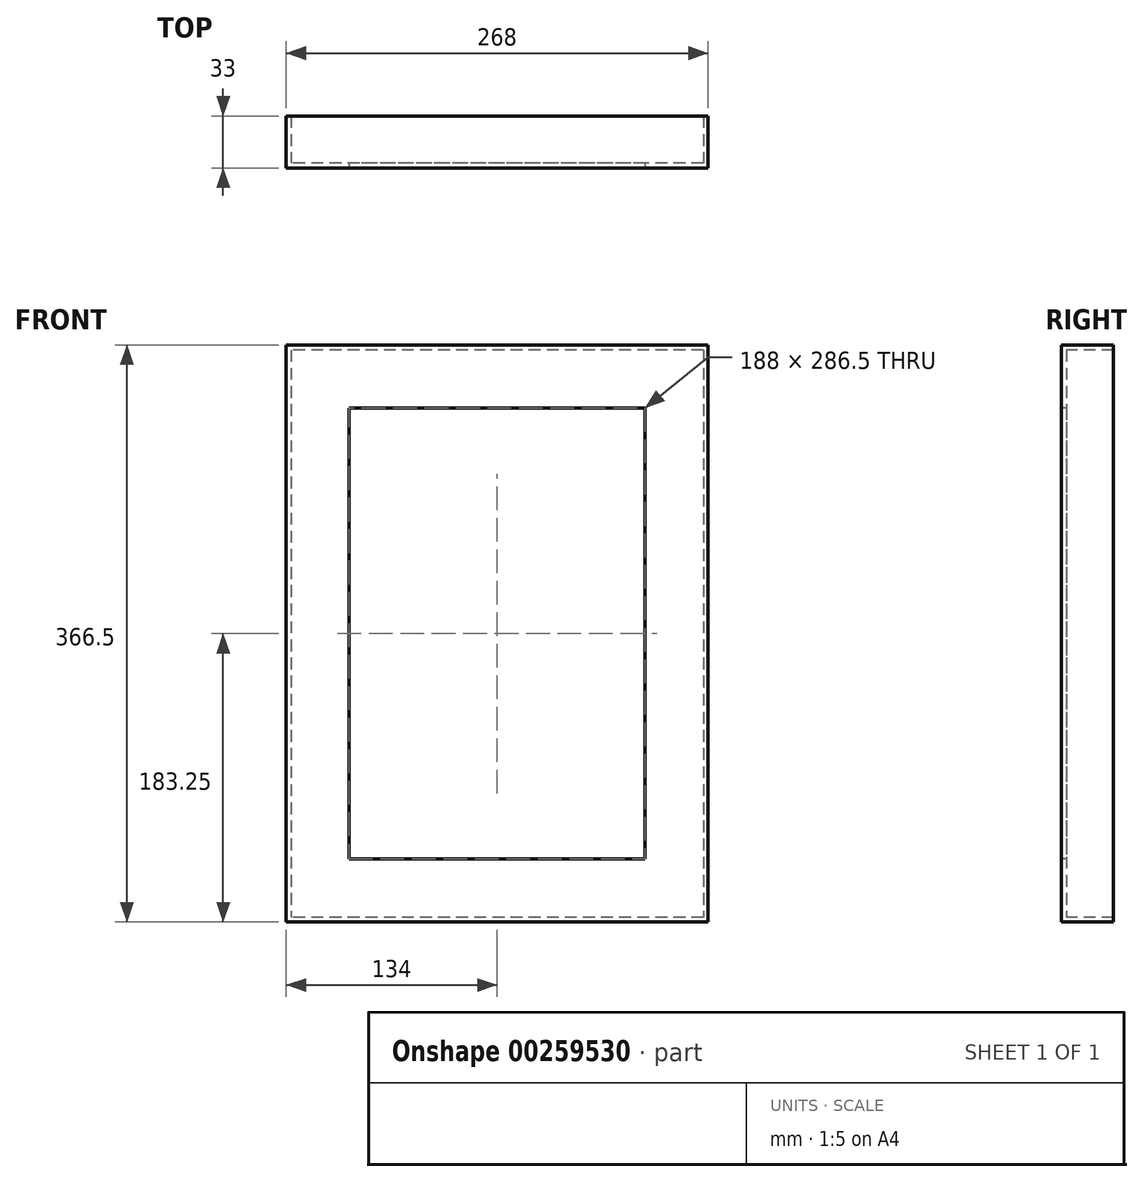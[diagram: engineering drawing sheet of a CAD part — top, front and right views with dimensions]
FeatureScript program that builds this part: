
annotation { "Feature Type Name" : "Feature", "Feature Type Description" : "" }
export const myFeature = defineFeature(function(context is Context, id is Id, definition is map)
    precondition{}
    {
        {
            var Q0;
            Q0=qCreatedBy(makeId("Front.planeOp"),FACE);
            var sketch = newSketch(context, id + "F0", { "sketchPlane" : qUnion([Q0])});
            skLineSegment(sketch, "E0.bottom", {"start": v(94, 143.25) * mm, "end": v(-94, 143.25) * mm});
            skLineSegment(sketch, "E0.top", {"start": v(94, -143.25) * mm, "end": v(-94, -143.25) * mm});
            skLineSegment(sketch, "E0.left", {"start": v(94, 143.25) * mm, "end": v(94, -143.25) * mm});
            skLineSegment(sketch, "E0.right", {"start": v(-94, 143.25) * mm, "end": v(-94, -143.25) * mm});
            skPoint(sketch, "E0.middle", {"position": v(0, 0) * mm});
            skLineSegment(sketch, "E1.0", {"start": v(-134, 183.25) * mm, "end": v(-134, -183.25) * mm});
            skLineSegment(sketch, "E1.1", {"start": v(134, 183.25) * mm, "end": v(-134, 183.25) * mm});
            skLineSegment(sketch, "E1.2", {"start": v(134, 183.25) * mm, "end": v(134, -183.25) * mm});
            skLineSegment(sketch, "E1.3", {"start": v(134, -183.25) * mm, "end": v(-134, -183.25) * mm});
            skSolve(sketch);
        }
        {
            var Q0;
            Q0=makeQuery(id+"F0.imprint","IMPRINT",FACE,{"disambiguationData":[TD([[makeQuery(id+"F0.imprint","IMPRINT",EDGE,{"derivedFrom":sQuery(id+"F0.wireOp",EDGE,"E0.bottom")}),-1.0]])]});
            extrude(context, id + "F1", {"entities" : qUnion([Q0]), "oppositeDirection" : true, "depth" : 3 * mm});
        }
        {
            var Q0;
            Q0=makeQuery(id+"F1.opExtrude","CAP_FACE",FACE,{"disambiguationData":[OSD([sQuery(id+"F0.wireOp",EDGE,"E0.bottom"),sQuery(id+"F0.wireOp",EDGE,"E0.top"),sQuery(id+"F0.wireOp",EDGE,"E0.left"),sQuery(id+"F0.wireOp",EDGE,"E0.right"),sQuery(id+"F0.wireOp",EDGE,"E1.0"),sQuery(id+"F0.wireOp",EDGE,"E1.1"),sQuery(id+"F0.wireOp",EDGE,"E1.2"),sQuery(id+"F0.wireOp",EDGE,"E1.3")])],"isStart":false});
            var sketch = newSketch(context, id + "F2", { "sketchPlane" : qUnion([Q0])});
            skLineSegment(sketch, "E2.bottom", {"start": v(-134, 183.25) * mm, "end": v(134, 183.25) * mm});
            skLineSegment(sketch, "E2.top", {"start": v(-134, -183.25) * mm, "end": v(134, -183.25) * mm});
            skLineSegment(sketch, "E2.left", {"start": v(-134, 183.25) * mm, "end": v(-134, -183.25) * mm});
            skLineSegment(sketch, "E2.right", {"start": v(134, 183.25) * mm, "end": v(134, -183.25) * mm});
            skLineSegment(sketch, "E3.0", {"start": v(-131, 180.25) * mm, "end": v(131, 180.25) * mm});
            skLineSegment(sketch, "E3.1", {"start": v(-131, 180.25) * mm, "end": v(-131, -180.25) * mm});
            skLineSegment(sketch, "E3.2", {"start": v(-131, -180.25) * mm, "end": v(131, -180.25) * mm});
            skLineSegment(sketch, "E3.3", {"start": v(131, 180.25) * mm, "end": v(131, -180.25) * mm});
            skSolve(sketch);
        }
        {
            var Q0;
            Q0=makeQuery(id+"F2.imprint","IMPRINT",FACE,{"disambiguationData":[TD([[makeQuery(id+"F2.imprint","IMPRINT",EDGE,{"derivedFrom":sQuery(id+"F2.wireOp",EDGE,"E2.bottom")}),-1.0]])]});
            extrude(context, id + "F3", {"entities" : qUnion([Q0]), "operationType" : NewBodyOperationType.ADD, "depth" : 30 * mm});
        }
    });
